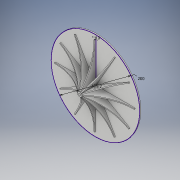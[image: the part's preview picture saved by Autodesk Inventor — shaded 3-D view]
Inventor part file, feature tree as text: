
AUTODESK INVENTOR PART (.ipt)
format: ipt  version: 2019.3 (Build 233278000, 278)  size: 207,872 bytes
history: native  units: mm
features: extrude x4, sketch x3, other x1, pattern_circular x1
ambient origin geometry x8: Origin, YZ Plane, XZ Plane, XY Plane, X Axis, Y Axis, Z Axis, Center Point
bodies: Solid1 (feature_tree)
feature tree (9):
  sketch  "Sketch1"  dims[d0=5.2mm d1=200.0mm]
  extrude  "Extrusion1"  Depth=200.0mm
  extrude  "Extrusion2"  Depth=2.0mm
  other  "Work Axis1"
  extrude  "Extrusion3"  Depth=10.0mm TaperAngle=0.0deg
  pattern_circular  "Circular Pattern1"  [2 undecoded]
  extrude  "Extrusion4"  Depth=2.0mm
  sketch  "Sketch2"  dims[d2=2.0mm d3=1.0mm]
  sketch  "Sketch3"  dims[d4=10.0mm d5=3.0mm d6=0.0mm d7=35.0mm d8=0.0mm d9=2.0mm d10=2.0mm d11=20.0mm d12=0.0mm d13=120.0mm d14=360.0deg d17=1.0mm d18=0.0mm d19=10.0mm d22=3.0mm d23=2.2mm]
note: 2 required parameter values undecoded (feature->parameter linkage not recoverable at this tier; creation-order binding heuristic only, values carry confidence <= 0.55)
